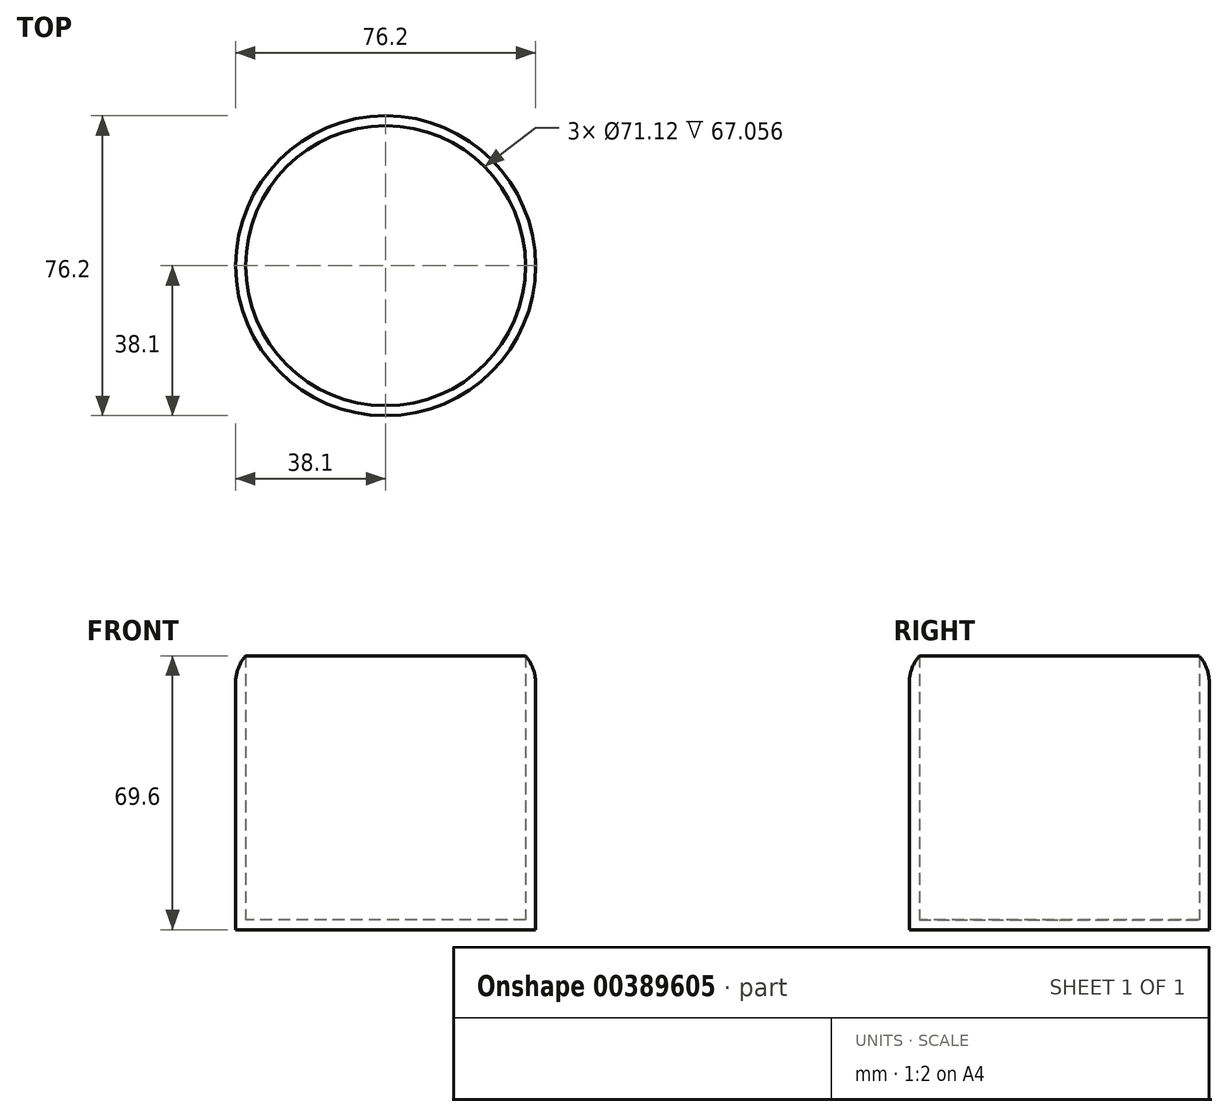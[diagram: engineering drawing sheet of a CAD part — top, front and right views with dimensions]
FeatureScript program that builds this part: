
annotation { "Feature Type Name" : "Feature", "Feature Type Description" : "" }
export const myFeature = defineFeature(function(context is Context, id is Id, definition is map)
    precondition{}
    {
        {
            var Q0;
            Q0=qCreatedBy(makeId("Top.planeOp"),FACE);
            var sketch = newSketch(context, id + "F0", { "sketchPlane" : qUnion([Q0])});
            skCircle(sketch, "E0", {"center": v(0, 0) * mm, "radius": 38.1 * mm});
            skSolve(sketch);
        }
        {
            var Q0;
            Q0=makeQuery(id+"F0.imprint","IMPRINT",FACE,{"disambiguationData":[TD([[makeQuery(id+"F0.imprint","IMPRINT",EDGE,{"derivedFrom":sQuery(id+"F0.wireOp",EDGE,"E0")}),1.0]])]});
            extrude(context, id + "F1", {"entities" : qUnion([Q0]), "endBound" : BoundingType.SYMMETRIC, "depth" : 69.6 * mm});
        }
        {
            var Q0;
            Q0=makeQuery(id+"F1.opExtrude","CAP_FACE",FACE,{"disambiguationData":[OSD([sQuery(id+"F0.wireOp",EDGE,"E0")])],"isStart":false});
            shell(context, id + "F2", {"entities" : qUnion([Q0]), "thickness" : 2.54 * mm});
        }
        {
            var Q0;
            Q0=makeQuery(id+"F1.opExtrude","CAP_EDGE",EDGE,{"disambiguationData":[OSD([sQuery(id+"F0.wireOp",EDGE,"E0")])],"isStart":false});
            fillet(context, id + "F3", {"entities" : qUnion([Q0]), "radius" : 10.42 * mm, "tangentPropagation" : true, "allowEdgeOverflow" : false});
        }
        {
            var Q0;
            Q0=qCreatedBy(makeId("Front.planeOp"),FACE);
            var sketch = newSketch(context, id + "F4", { "sketchPlane" : qUnion([Q0])});
            skArc(sketch, "E1", {"start": v(37.84, -25.82) * mm, "mid": v(52.93, -5.07) * mm, "end": v(38.23, 15.96) * mm});
            skArc(sketch, "E2", {"start": v(38.23, -28.18) * mm, "mid": v(58.6, -4.53) * mm, "end": v(38.23, 19.12) * mm});
            skSolve(sketch);
        }
        {
            var Q0;
            Q0=sQuery(id+"F4.wireOp",EDGE,"E2");
            var Q1;
            Q1=sQuery(id+"F4.wireOp",EDGE,"E1");
            extrude(context, id + "F5", {"bodyType" : ToolBodyType.SURFACE, "surfaceEntities" : qUnion([Q0, Q1]), "endBound" : BoundingType.SYMMETRIC, "depth" : 14.73 * mm});
        }
    });
